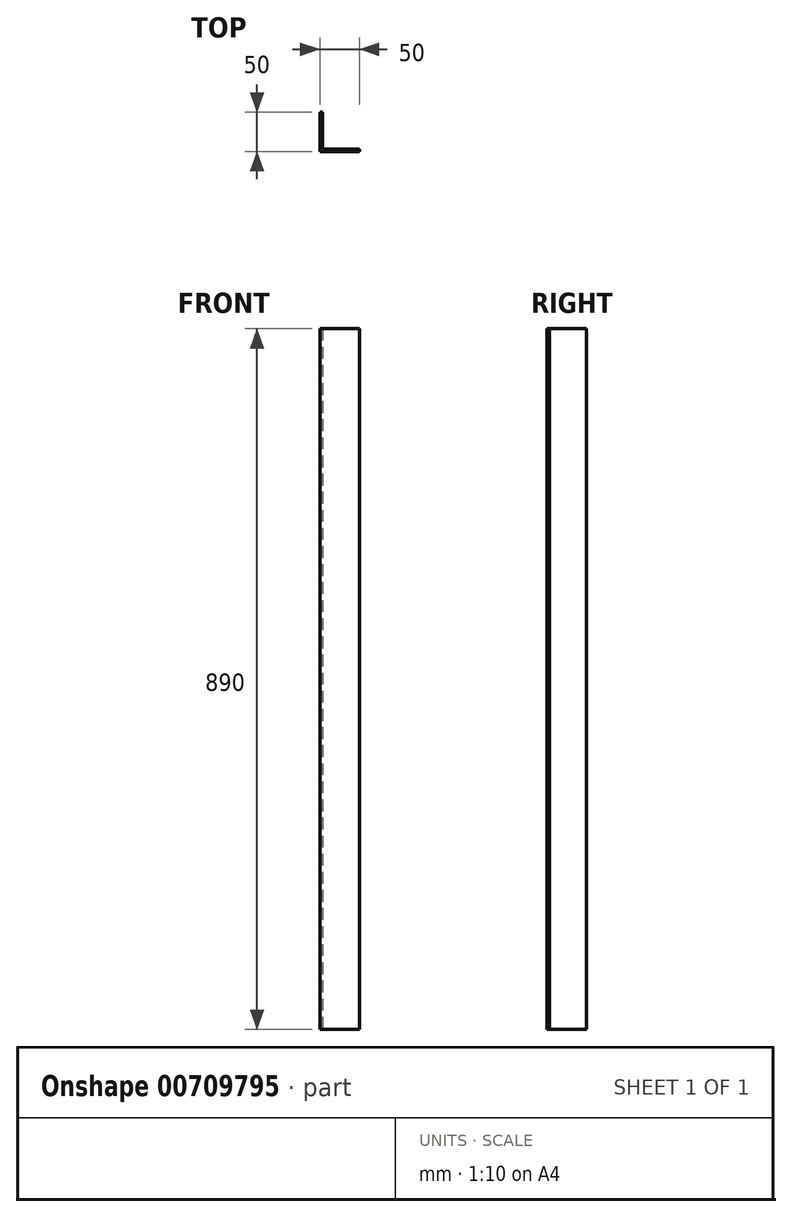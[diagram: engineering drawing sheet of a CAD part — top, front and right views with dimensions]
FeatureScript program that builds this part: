
annotation { "Feature Type Name" : "Feature", "Feature Type Description" : "" }
export const myFeature = defineFeature(function(context is Context, id is Id, definition is map)
    precondition{}
    {
        {
            var Q0;
            Q0=qCreatedBy(makeId("Top.planeOp"),FACE);
            var sketch = newSketch(context, id + "F0", { "sketchPlane" : qUnion([Q0])});
            skLineSegment(sketch, "E0.bottom", {"start": v(-77.52, -54.25) * mm, "end": v(-27.52, -54.25) * mm});
            skLineSegment(sketch, "E0.top", {"start": v(-77.52, -4.25) * mm, "end": v(-74.52, -4.25) * mm});
            skLineSegment(sketch, "E0.left", {"start": v(-77.52, -54.25) * mm, "end": v(-77.52, -4.25) * mm});
            skLineSegment(sketch, "E0.right", {"start": v(-27.52, -54.25) * mm, "end": v(-27.52, -51.25) * mm});
            skLineSegment(sketch, "E1.1", {"start": v(-74.52, -51.25) * mm, "end": v(-74.52, -4.25) * mm});
            skLineSegment(sketch, "E1.2", {"start": v(-74.52, -51.25) * mm, "end": v(-27.52, -51.25) * mm});
            skSolve(sketch);
        }
        {
            var Q0;
            Q0 = qSketchRegion(id + "F0", true);
            extrude(context, id + "F1", {"entities" : qUnion([Q0]), "depth" : 890 * mm, "offsetDistance" : 25 * mm});
        }
    });
